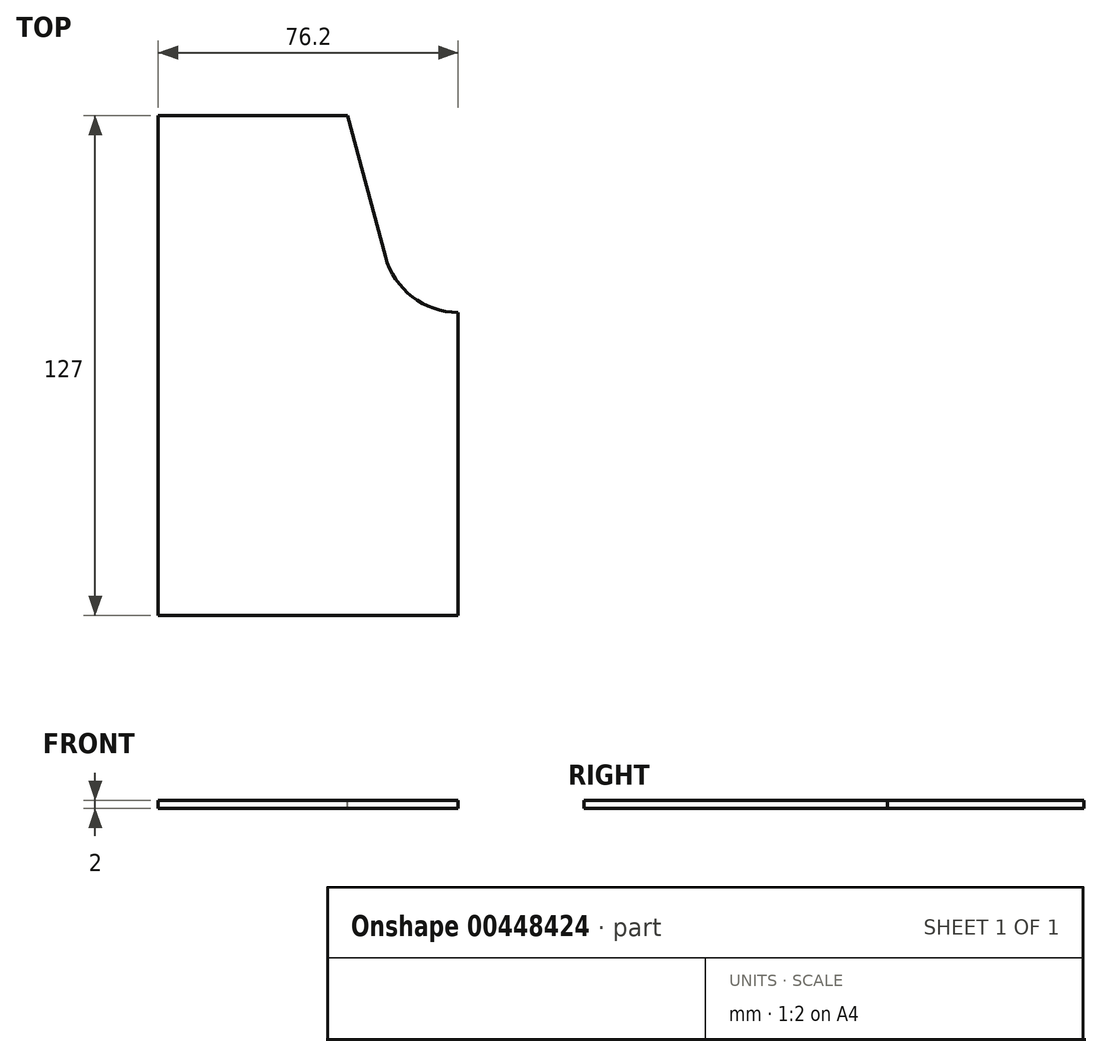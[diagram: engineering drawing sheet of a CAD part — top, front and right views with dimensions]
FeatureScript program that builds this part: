
annotation { "Feature Type Name" : "Feature", "Feature Type Description" : "" }
export const myFeature = defineFeature(function(context is Context, id is Id, definition is map)
    precondition{}
    {
        {
            var Q0;
            Q0=qCreatedBy(makeId("Top.planeOp"),FACE);
            var sketch = newSketch(context, id + "F0", { "sketchPlane" : qUnion([Q0])});
            skLineSegment(sketch, "E0.bottom", {"start": v(38.1, 63.5) * mm, "end": v(-38.1, 63.5) * mm});
            skLineSegment(sketch, "E0.top", {"start": v(38.1, -63.5) * mm, "end": v(-38.1, -63.5) * mm});
            skLineSegment(sketch, "E0.left", {"start": v(38.1, 63.5) * mm, "end": v(38.1, -63.5) * mm});
            skLineSegment(sketch, "E0.right", {"start": v(-38.1, 63.5) * mm, "end": v(-38.1, -63.5) * mm});
            skPoint(sketch, "E0.middle", {"position": v(0, 0) * mm});
            skSolve(sketch);
        }
        {
            var Q0;
            Q0=makeQuery(id+"F0.imprint","IMPRINT",FACE,{"disambiguationData":[TD([[makeQuery(id+"F0.imprint","IMPRINT",EDGE,{"derivedFrom":sQuery(id+"F0.wireOp",EDGE,"E0.bottom")}),1.0]])]});
            extrude(context, id + "F1", {"entities" : qUnion([Q0]), "depth" : 2 * mm});
        }
        {
            var Q0;
            Q0=makeQuery(id+"F1.opExtrude","CAP_FACE",FACE,{"disambiguationData":[OSD([sQuery(id+"F0.wireOp",EDGE,"E0.bottom"),sQuery(id+"F0.wireOp",EDGE,"E0.top"),sQuery(id+"F0.wireOp",EDGE,"E0.left"),sQuery(id+"F0.wireOp",EDGE,"E0.right")])],"isStart":false});
            var sketch = newSketch(context, id + "F2", { "sketchPlane" : qUnion([Q0])});
            skLineSegment(sketch, "E1", {"start": v(10, 63.5) * mm, "end": v(19.6, 27.7) * mm});
            skArc(sketch, "E2", {"start": v(19.6, 27.7) * mm, "mid": v(26.44, 17.46) * mm, "end": v(38.1, 13.5) * mm});
            skLineSegment(sketch, "E3.0", {"start": v(38.1, 63.5) * mm, "end": v(38.1, -63.5) * mm});
            skLineSegment(sketch, "E4.0", {"start": v(38.1, 63.5) * mm, "end": v(-38.1, 63.5) * mm});
            skLineSegment(sketch, "E5", {"start": v(-12.33, 63.5) * mm, "end": v(-20.89, 19.6) * mm});
            skArc(sketch, "E6", {"start": v(-38.1, 0) * mm, "mid": v(-26.84, 7.47) * mm, "end": v(-20.89, 19.6) * mm});
            skLineSegment(sketch, "E7", {"start": v(0, 0) * mm, "end": v(0, 70.1) * mm});
            skSolve(sketch);
        }
        {
            var Q0;
            {var subQ0=sQuery(id+"F2.wireOp",EDGE,"E1");Q0=makeQuery(id+"F2.imprint","IMPRINT",FACE,{"disambiguationData":[TD([[makeQuery(id+"F2.imprint","IMPRINT",EDGE,{"derivedFrom":subQ0}),1.0]])]});}
            extrude(context, id + "F3", {"entities" : qUnion([Q0]), "operationType" : NewBodyOperationType.REMOVE, "oppositeDirection" : true, "depth" : 25 * mm});
        }
    });
